# Revit family: NBS_Senator_MeetingPods_SoloAbodeLodge
name_source: partatom
category: Furniture
revit_build: Autodesk Revit 2018 (Build: 20190510_1515(x64)
units: mm (PartAtom-declared; Revit-internal decimal feet)

## family parameters
Always vertical = Yes
Cut with Voids When Loaded = No
Room Calculation Point = No
Shared = No
Work Plane-Based = No

## types (2) — shared parameters
Accessories = Monitor arms, PU desk accessories, desk top accessories, CPU holders, electrical accessories, coat hanger, name plate, A2 dry wipe board with hanger, A3 dry wipe board with hanger
AssetType = Fixed
Category = Pr_40_50_12_53:Meeting pods
Description = Large single person workspace comprising ten mid height panel
DeskMaterial = NBS_Senator_Wood_Dark_Mocha
DeskStructureMaterial = NBS_Senator_Aluminium_Flat_Silver
DurationUnit = year
ExpectedLife = 10
FabricFinishOptions = Plymouth, fairfield, latymer, lancaster, silcoates, silverdale, st andrews, trevelyan, ulster, wellington, wesley, manchester,
Features = Internal frame with multi-layered acoustic foam, levelling adjusters, blazer fabric, outer vertical panels
Finish = Outer vertical panels upholstered in camira, blazer fabric Two tone is standard
FinishOptions = Carini walnut, mocha, autumn, strata oak, maple, highland oak, beech, winter oak, hacienda white, white, light grey, denim, clay, lemon sorbet
FramesColour = Black, white
IfcExportAs = IfcFurnitureType
IfcExportType = USERDEFINED
InnerPanelMaterial = NBS_Senator_VirginWool_StAndrews
IsBuiltIn = No
ManufacturerName = The Senator Group
ManufacturerURL = www.senator.co.uk
Material = Fabric, metal, plastic
MiddlePanelMaterial = NBS_Senator_Aluminium_Rigid_Silver
NBSCertification = www.nationalbimlibrary.com/cert/ey5ogywm
NBSDescription = Meeting pods
NBSReference = 45-35-20/342
NominalDepth = 3000 mm  [stored 9.84252 ft]
NominalLength = 2000 mm  [stored 6.56168 ft]
OuterPanelMaterial = NBS_Senator_VirginWool_Fairfield
PodDepth = 3000 mm  [stored 9.84252 ft]
PodWidth = 2000 mm  [stored 6.56168 ft]
SeatBackMaterial = NBS_Senator_VirginWool_Wellington
SeatMaterial = NBS_Senator_VirginWool_Wellington
Status = UNSET
StorageFrontMaterial = NBS_Senator_Wood_White
StoragePanelMaterial = NBS_Senator_Wood_White
StorageTopMaterial = NBS_Senator_Wood_Dark_Mocha
Style = Pods
SustainabilityPerformance = 99% recyclable
Uniclass2015Code = Pr_40_50_12_53
Uniclass2015Title = Meeting pods
Uniclass2015Version = Products v1.16
Version = 1
WarrantyDescription = Senator warrants that its manufactured products are free from manufacturing defects - in materials or workmanship - for a period of ten (10) years on Senator Seating ranges; and fifteen (15) years on Senator Desking ranges - exceptions are listed below. Senator will repair or replace (at Senator’s sole discretion) with comparable free of charge materials / components, any product / component, which fails under normal use in a single shift environment, as a result of a defect in the materials and / or workmanship
WarrantyDurationParts = 10
WarrantyDurationUnit = year

## per-type parameters (varying)
| type | BIMObjectName | ModelReference | Name | NominalHeight | NominalWidth | PodHeight | Size |
| PDSL14 | NBS_Senator_MeetingPods_SoloLodge_PDSL14 | Pods-SoloLodge_PDSL14 | MeetingPods_SoloLodge_PDSL14_Senator | 1400 mm  [stored 4.59318 ft] | 1400 mm  [stored 4.59318 ft] | 1400 mm  [stored 4.59318 ft] | 3000 x 2000 x 1400 mm |
| PDSL18 | NBS_Senator_MeetingPods_SoloLodge_PDSL18 | Pods-SoloLodge_PDSL18 | MeetingPods_SoloLodge_PDSL18_Senator | 1800 mm  [stored 5.90551 ft] | 1800 mm  [stored 5.90551 ft] | 1800 mm  [stored 5.90551 ft] | 3000 x 2000 x 1800 mm |

note: column(s) folded — value = type name in every type: ModelNumber

note: [stored X ft] marks values corroborated as IEEE doubles in the binary element streams (Revit-internal decimal feet)

## geometry (parser evidence)
native form markers: Sweep x8
no freeform markers — native parametric forms only
